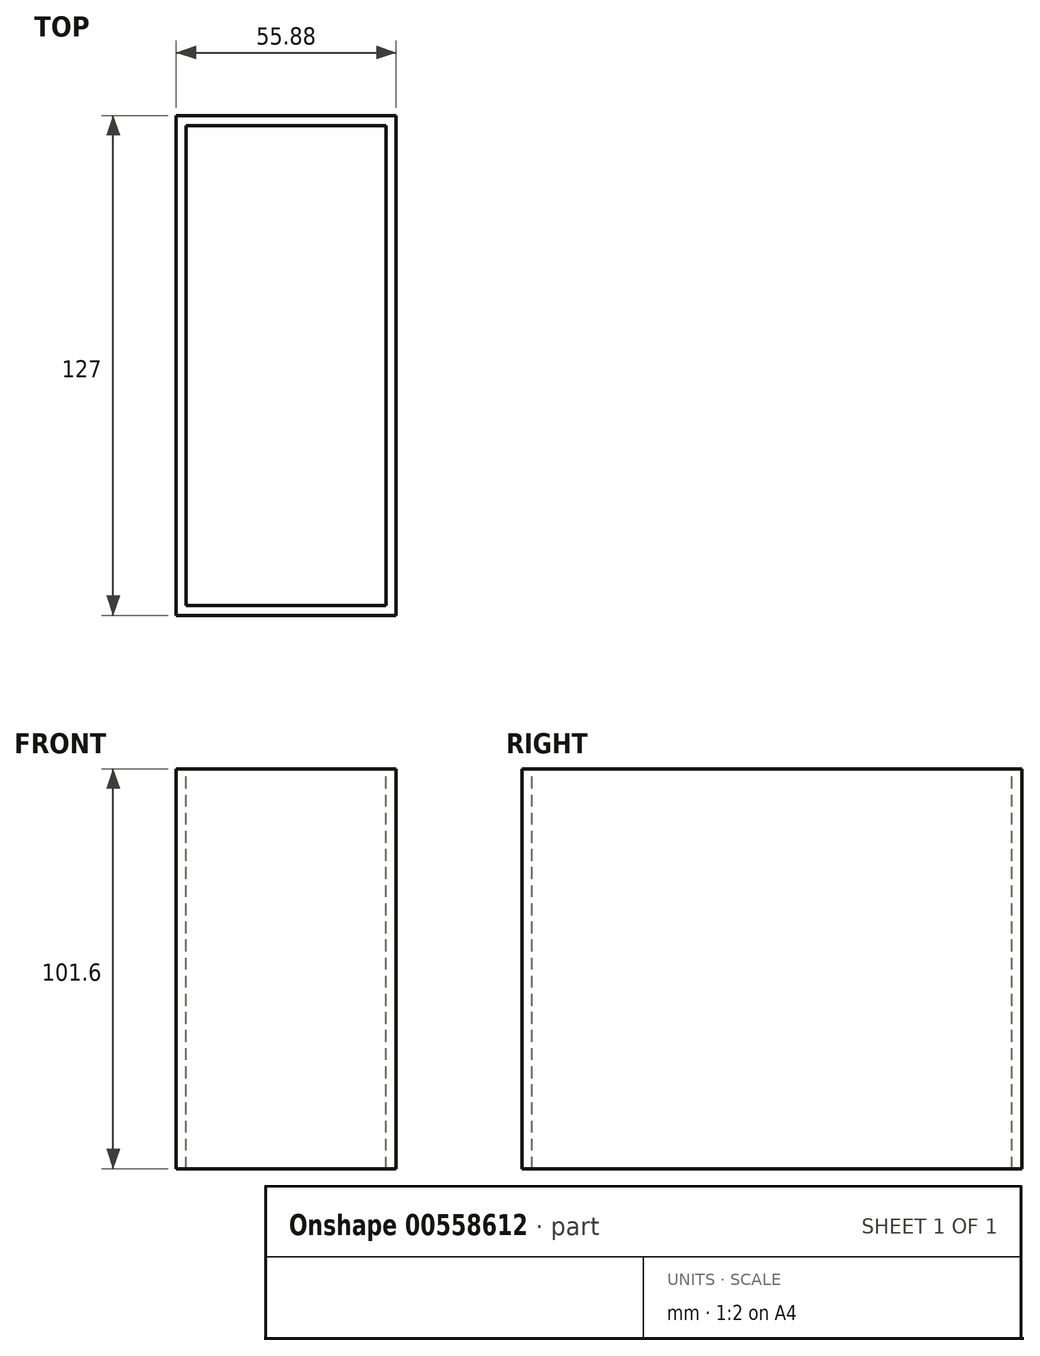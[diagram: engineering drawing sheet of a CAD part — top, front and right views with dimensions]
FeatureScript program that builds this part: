
annotation { "Feature Type Name" : "Feature", "Feature Type Description" : "" }
export const myFeature = defineFeature(function(context is Context, id is Id, definition is map)
    precondition{}
    {
        {
            var Q0;
            Q0=qCreatedBy(makeId("Front.planeOp"),FACE);
            var sketch = newSketch(context, id + "F0", { "sketchPlane" : qUnion([Q0])});
            skLineSegment(sketch, "E0.bottom", {"start": v(0, 0) * mm, "end": v(-55.88, 0) * mm});
            skLineSegment(sketch, "E0.top", {"start": v(0, 101.6) * mm, "end": v(-55.88, 101.6) * mm});
            skLineSegment(sketch, "E0.left", {"start": v(0, 0) * mm, "end": v(0, 101.6) * mm});
            skLineSegment(sketch, "E0.right", {"start": v(-55.88, 0) * mm, "end": v(-55.88, 101.6) * mm});
            skSolve(sketch);
        }
        {
            var Q0;
            Q0=makeQuery(id+"F0.imprint","IMPRINT",FACE,{"disambiguationData":[TD([[makeQuery(id+"F0.imprint","IMPRINT",EDGE,{"derivedFrom":sQuery(id+"F0.wireOp",EDGE,"E0.bottom")}),-1.0]])]});
            extrude(context, id + "F1", {"entities" : qUnion([Q0]), "depth" : 127 * mm, "offsetDistance" : 25.4 * mm});
        }
        {
            var Q0;
            Q0=makeQuery(id+"F1.opExtrude","SWEPT_FACE",FACE,{"disambiguationData":[OSD([sQuery(id+"F0.wireOp",EDGE,"E0.top")])]});
            var Q1;
            Q1=makeQuery(id+"F1.opExtrude","SWEPT_FACE",FACE,{"disambiguationData":[OSD([sQuery(id+"F0.wireOp",EDGE,"E0.bottom")])]});
            shell(context, id + "F2", {"entities" : qUnion([Q0, Q1]), "thickness" : 2.54 * mm});
        }
    });
